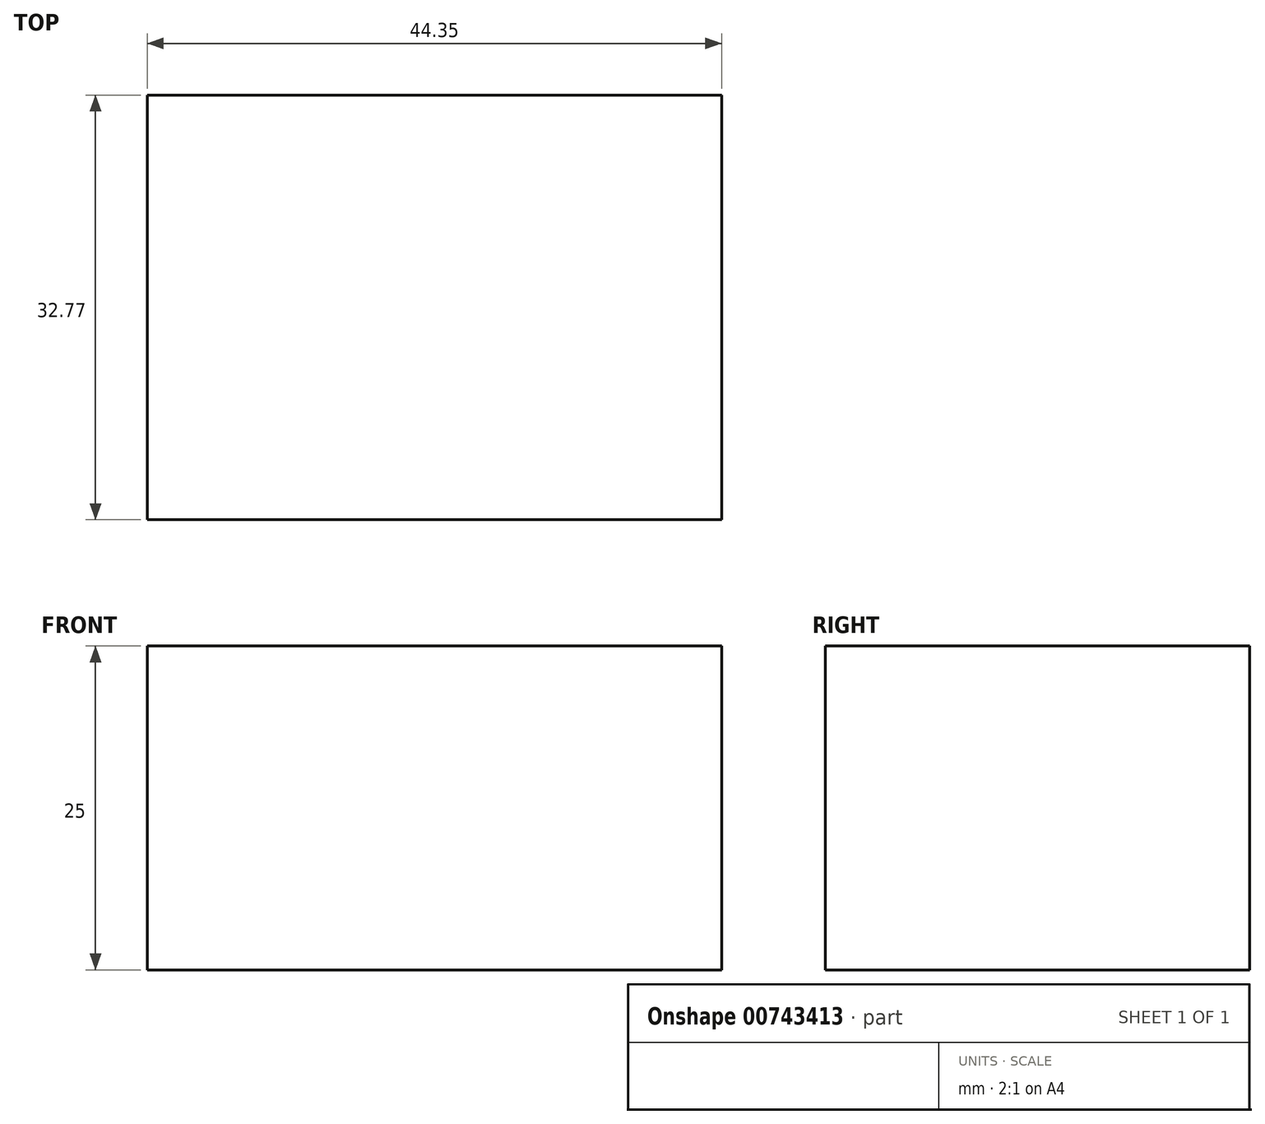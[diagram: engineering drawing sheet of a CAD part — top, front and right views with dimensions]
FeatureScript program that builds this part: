
annotation { "Feature Type Name" : "Feature", "Feature Type Description" : "" }
export const myFeature = defineFeature(function(context is Context, id is Id, definition is map)
    precondition{}
    {
        {
            var Q0;
            Q0=qCreatedBy(makeId("Top.planeOp"),FACE);
            var sketch = newSketch(context, id + "F0", { "sketchPlane" : qUnion([Q0])});
            skLineSegment(sketch, "E0.bottom", {"start": v(0, 0) * mm, "end": v(44.35, 0) * mm});
            skLineSegment(sketch, "E0.top", {"start": v(0, 32.77) * mm, "end": v(44.35, 32.77) * mm});
            skLineSegment(sketch, "E0.left", {"start": v(0, 0) * mm, "end": v(0, 32.77) * mm});
            skLineSegment(sketch, "E0.right", {"start": v(44.35, 0) * mm, "end": v(44.35, 32.77) * mm});
            skSolve(sketch);
        }
        {
            var Q0;
            Q0=makeQuery(id+"F0.imprint","IMPRINT",FACE,{"disambiguationData":[TD([[makeQuery(id+"F0.imprint","IMPRINT",EDGE,{"derivedFrom":sQuery(id+"F0.wireOp",EDGE,"E0.bottom")}),1.0]])]});
            extrude(context, id + "F1", {"entities" : qUnion([Q0]), "depth" : 25 * mm, "offsetDistance" : 25 * mm});
        }
    });
